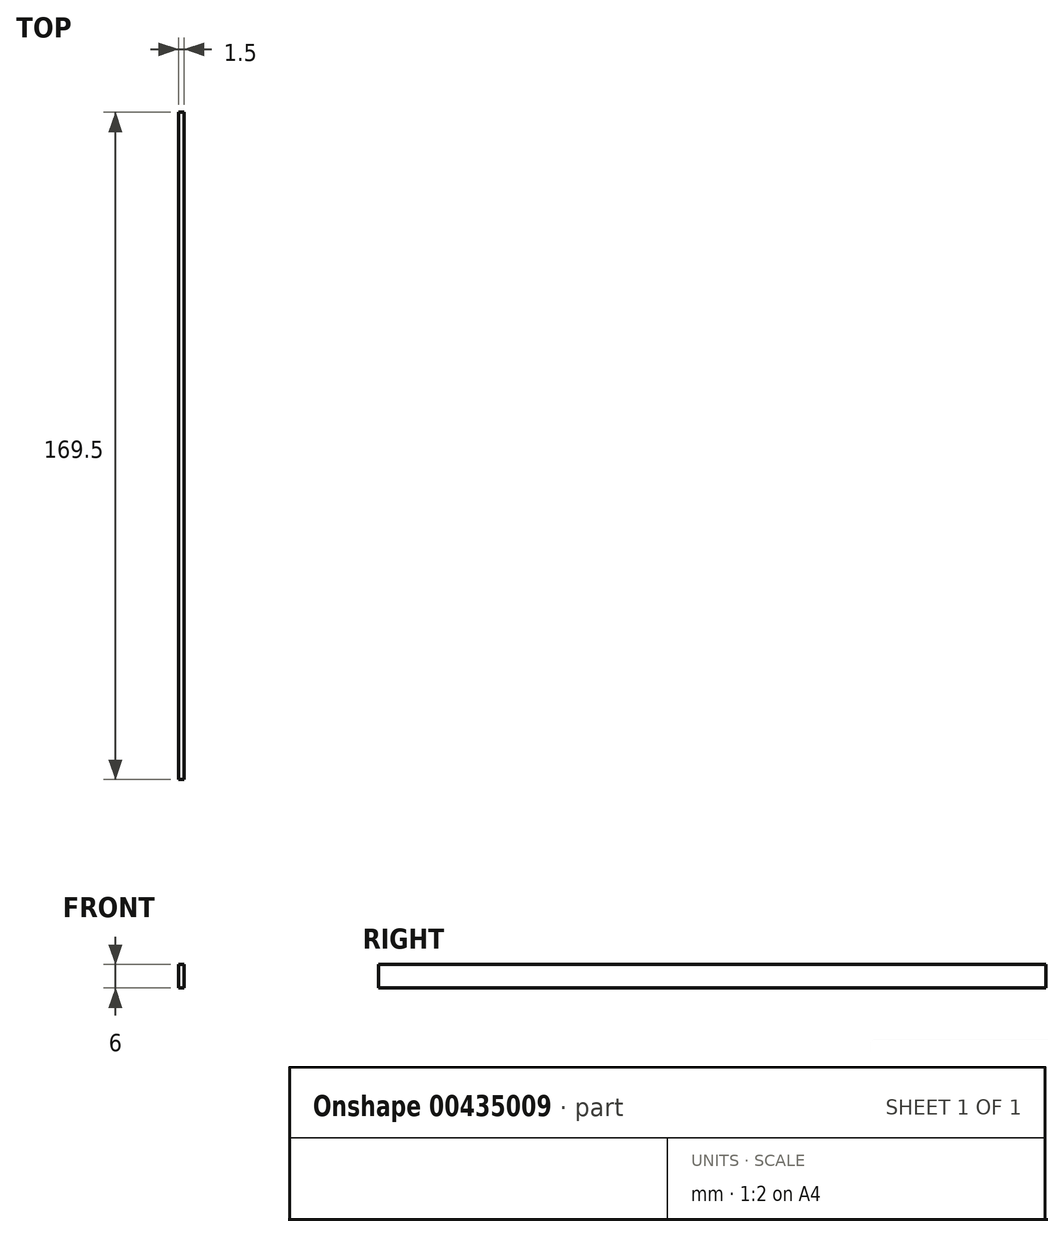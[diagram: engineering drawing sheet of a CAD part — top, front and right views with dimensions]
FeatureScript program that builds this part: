
annotation { "Feature Type Name" : "Feature", "Feature Type Description" : "" }
export const myFeature = defineFeature(function(context is Context, id is Id, definition is map)
    precondition{}
    {
        {
            var Q0;
            Q0=qCreatedBy(makeId("Right.planeOp"),FACE);
            var sketch = newSketch(context, id + "F0", { "sketchPlane" : qUnion([Q0])});
            skLineSegment(sketch, "E0.bottom", {"start": v(0, 0) * mm, "end": v(169.5, 0) * mm});
            skLineSegment(sketch, "E0.top", {"start": v(0, 6) * mm, "end": v(169.5, 6) * mm});
            skLineSegment(sketch, "E0.left", {"start": v(0, 0) * mm, "end": v(0, 6) * mm});
            skLineSegment(sketch, "E0.right", {"start": v(169.5, 0) * mm, "end": v(169.5, 6) * mm});
            skSolve(sketch);
        }
        {
            var Q0;
            Q0 = qSketchRegion(id + "F0", true);
            extrude(context, id + "F1", {"entities" : qUnion([Q0]), "depth" : 1.5 * mm});
        }
    });
